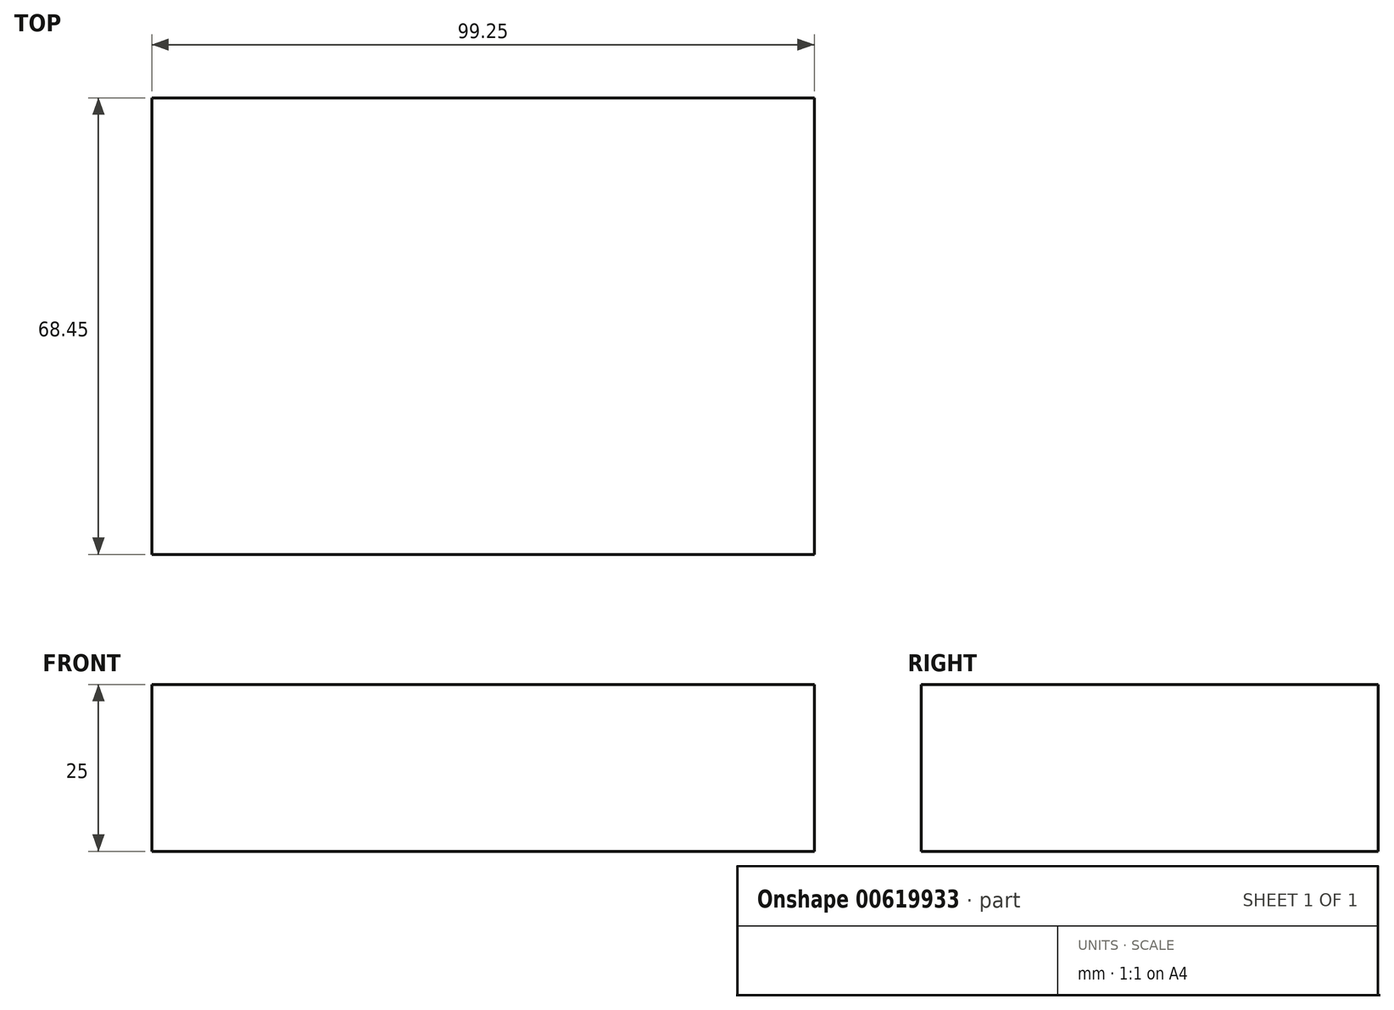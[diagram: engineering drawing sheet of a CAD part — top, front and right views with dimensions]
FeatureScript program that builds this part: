
annotation { "Feature Type Name" : "Feature", "Feature Type Description" : "" }
export const myFeature = defineFeature(function(context is Context, id is Id, definition is map)
    precondition{}
    {
        {
            var Q0;
            Q0=qCreatedBy(makeId("Top.planeOp"),FACE);
            var sketch = newSketch(context, id + "F0", { "sketchPlane" : qUnion([Q0])});
            skLineSegment(sketch, "E0.bottom", {"start": v(-52.07, 35.7) * mm, "end": v(47.18, 35.7) * mm});
            skLineSegment(sketch, "E0.top", {"start": v(-52.07, -32.76) * mm, "end": v(47.18, -32.76) * mm});
            skLineSegment(sketch, "E0.left", {"start": v(-52.07, 35.7) * mm, "end": v(-52.07, -32.76) * mm});
            skLineSegment(sketch, "E0.right", {"start": v(47.18, 35.7) * mm, "end": v(47.18, -32.76) * mm});
            skSolve(sketch);
        }
        {
            var Q0;
            Q0=makeQuery(id+"F0.imprint","IMPRINT",FACE,{"disambiguationData":[TD([[makeQuery(id+"F0.imprint","IMPRINT",EDGE,{"derivedFrom":sQuery(id+"F0.wireOp",EDGE,"E0.bottom")}),-1.0]])]});
            extrude(context, id + "F1", {"entities" : qUnion([Q0]), "depth" : 25 * mm, "offsetDistance" : 25 * mm});
        }
    });
